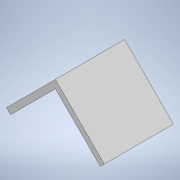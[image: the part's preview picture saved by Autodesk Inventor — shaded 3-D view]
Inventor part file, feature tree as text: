
AUTODESK INVENTOR PART (.ipt)
format: ipt  version: 2022 (Build 260153000, 153)  size: 232,960 bytes
history: native  units: in
note: dims shown in document units (in); Inventor stores cm internally (conversion verified against a paired STEP export)
features: extrude x2, sketch x2
ambient origin geometry x8: Origin, YZ Plane, XZ Plane, XY Plane, X Axis, Y Axis, Z Axis, Center Point
bodies: Solid1 (feature_tree)
feature tree (4):
  extrude  "Extrusion1"  TaperAngle=45.0deg  [1 undecoded]
  extrude  "Extrusion2"  Depth=0.9843in
  sketch  "Sketch1"  dims[d2=11.811in d3=45.0deg]
  sketch  "Sketch3"  dims[d4=11.811in d5=0.9843in d6=11.811in d7=0.0in d8=1.1811in d9=0.1969in d10=0.0in]
note: 1 required parameter value undecoded (feature->parameter linkage not recoverable at this tier; creation-order binding heuristic only, values carry confidence <= 0.55)
